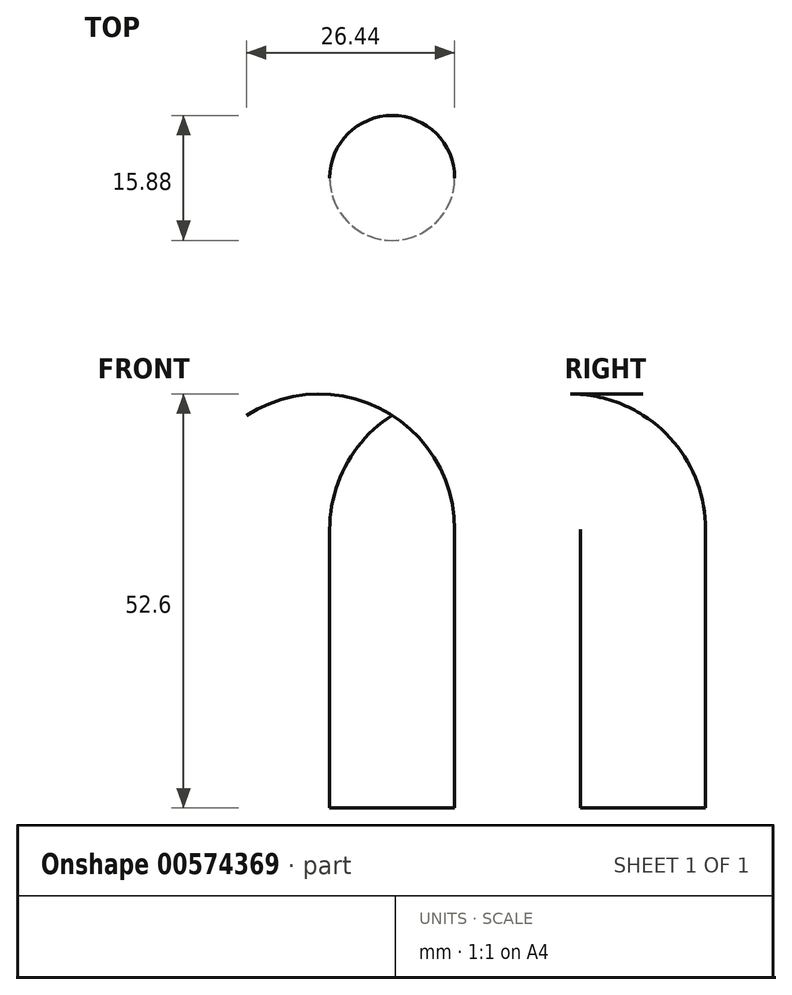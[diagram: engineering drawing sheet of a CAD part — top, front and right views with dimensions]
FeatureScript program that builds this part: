
annotation { "Feature Type Name" : "Feature", "Feature Type Description" : "" }
export const myFeature = defineFeature(function(context is Context, id is Id, definition is map)
    precondition{}
    {
        {
            var Q0;
            Q0=qCreatedBy(makeId("Right.planeOp"),FACE);
            var sketch = newSketch(context, id + "F0", { "sketchPlane" : qUnion([Q0])});
            skLineSegment(sketch, "E0.bottom", {"start": v(0, 0) * mm, "end": v(7.94, 0) * mm});
            skLineSegment(sketch, "E0.top", {"start": v(0, 35.4) * mm, "end": v(7.94, 35.4) * mm});
            skLineSegment(sketch, "E0.left", {"start": v(0, 0) * mm, "end": v(0, 35.4) * mm});
            skLineSegment(sketch, "E0.right", {"start": v(7.94, 0) * mm, "end": v(7.94, 35.4) * mm});
            skLineSegment(sketch, "E1", {"start": v(0, 35.4) * mm, "end": v(0, 49.9) * mm});
            skArc(sketch, "E2", {"start": v(7.94, 35.4) * mm, "mid": v(5.83, 43.67) * mm, "end": v(0, 49.9) * mm});
            skSolve(sketch);
        }
        {
            var Q0;
            Q0=makeQuery(id+"F0.imprint","IMPRINT",FACE,{"disambiguationData":[TD([[makeQuery(id+"F0.imprint","IMPRINT",EDGE,{"derivedFrom":sQuery(id+"F0.wireOp",EDGE,"E0.top")}),1.0]])]});
            var Q1;
            Q1=makeQuery(id+"F0.imprint","IMPRINT",FACE,{"disambiguationData":[TD([[makeQuery(id+"F0.imprint","IMPRINT",EDGE,{"derivedFrom":sQuery(id+"F0.wireOp",EDGE,"E0.bottom")}),1.0]])]});
            var Q2;
            Q2=sQuery(id+"F0.wireOp",EDGE,"E0.left");
            revolve(context, id + "F1", {"entities" : qUnion([Q0, Q1]), "axis" : qUnion([Q2]), "revolveType" : RevolveType.FULL});
        }
    });
